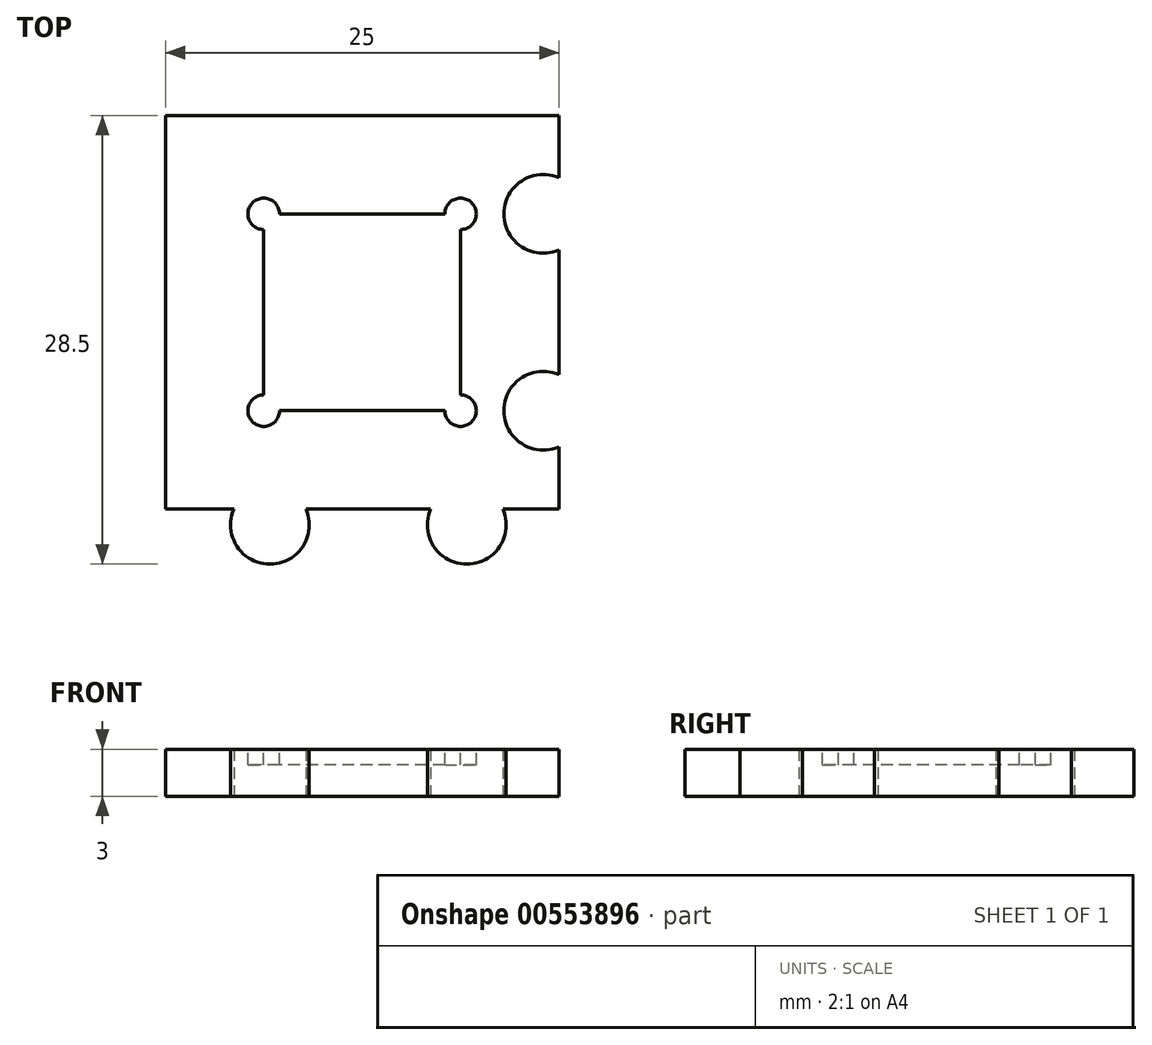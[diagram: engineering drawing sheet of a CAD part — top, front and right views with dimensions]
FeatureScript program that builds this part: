
annotation { "Feature Type Name" : "Feature", "Feature Type Description" : "" }
export const myFeature = defineFeature(function(context is Context, id is Id, definition is map)
    precondition{}
    {
        {
            var Q0;
            Q0=qCreatedBy(makeId("Top.planeOp"),FACE);
            var sketch = newSketch(context, id + "F0", { "sketchPlane" : qUnion([Q0])});
            skLineSegment(sketch, "E0.bottom", {"start": v(12.5, 12.5) * mm, "end": v(-12.5, 12.5) * mm});
            skLineSegment(sketch, "E0.top", {"start": v(12.5, -12.5) * mm, "end": v(-12.5, -12.5) * mm});
            skLineSegment(sketch, "E0.left", {"start": v(12.5, 12.5) * mm, "end": v(12.5, -12.5) * mm});
            skLineSegment(sketch, "E0.right", {"start": v(-12.5, 12.5) * mm, "end": v(-12.5, -12.5) * mm});
            skPoint(sketch, "E0.middle", {"position": v(0, 0) * mm});
            skCircle(sketch, "E1", {"center": v(-5.86, -13.5) * mm, "radius": 2.5 * mm});
            skCircle(sketch, "E2.1.0.0", {"center": v(6.64, -13.5) * mm, "radius": 2.5 * mm});
            skLineSegment(sketch, "E2.direction1", {"start": v(-5.86, -13.5) * mm, "end": v(6.64, -13.5) * mm, "construction": true});
            skSolve(sketch);
        }
        {
            var Q0;
            Q0=qSketchRegion(id+"F0",true);
            extrude(context, id + "F1", {"entities" : qUnion([Q0]), "depth" : 3 * mm, "offsetDistance" : 25 * mm});
        }
        {
            var Q0;
            Q0=makeQuery(id+"F1.opExtrude","CAP_FACE",FACE,{"disambiguationData":[OSD([sQuery(id+"F0.wireOp",EDGE,"E0.bottom"),sQuery(id+"F0.wireOp",EDGE,"E0.top"),sQuery(id+"F0.wireOp",EDGE,"E0.left"),sQuery(id+"F0.wireOp",EDGE,"E0.right")])],"isStart":false});
            var sketch = newSketch(context, id + "F2", { "sketchPlane" : qUnion([Q0])});
            skLineSegment(sketch, "E3.bottom", {"start": v(6.25, 6.25) * mm, "end": v(-6.25, 6.25) * mm});
            skLineSegment(sketch, "E3.top", {"start": v(6.25, -6.25) * mm, "end": v(-6.25, -6.25) * mm});
            skLineSegment(sketch, "E3.left", {"start": v(6.25, 6.25) * mm, "end": v(6.25, -6.25) * mm});
            skLineSegment(sketch, "E3.right", {"start": v(-6.25, 6.25) * mm, "end": v(-6.25, -6.25) * mm});
            skPoint(sketch, "E3.middle", {"position": v(0, 0) * mm});
            skCircle(sketch, "E4", {"center": v(-6.25, 6.25) * mm, "radius": 1 * mm});
            skCircle(sketch, "E5.0.1.0", {"center": v(-6.25, -6.25) * mm, "radius": 1 * mm});
            skCircle(sketch, "E5.1.0.0", {"center": v(6.25, 6.25) * mm, "radius": 1 * mm});
            skCircle(sketch, "E5.1.1.0", {"center": v(6.25, -6.25) * mm, "radius": 1 * mm});
            skLineSegment(sketch, "E5.direction1", {"start": v(-6.25, 6.25) * mm, "end": v(6.25, 6.25) * mm, "construction": true});
            skLineSegment(sketch, "E5.direction2", {"start": v(-6.25, 6.25) * mm, "end": v(-6.25, -6.25) * mm, "construction": true});
            skSolve(sketch);
        }
        {
            var Q0;
            {var subQ5=sQuery(id+"F2.wireOp",EDGE,"E5.1.0.0");var subQ13=sQuery(id+"F2.wireOp",EDGE,"E3.bottom");var subQ14=makeQuery(id+"F2.imprint","INTERSECT",VERTEX,{"derivedFrom":[subQ13,subQ5]});Q0=makeQuery(id+"F2.imprint","IMPRINT",FACE,{"disambiguationData":[TD([[makeQuery(id+"F2.imprint","IMPRINT",EDGE,{"disambiguationData":[TD([[subQ14,-1.0]])],"derivedFrom":subQ13}),1.0]])]});}
            var Q1;
            {var subQ0=sQuery(id+"F2.wireOp",EDGE,"E3.right");var subQ1=sQuery(id+"F2.wireOp",EDGE,"E3.bottom");var subQ2=makeQuery(id+"F2.imprint","INTERSECT",VERTEX,{"derivedFrom":[subQ1,subQ0]});Q1=makeQuery(id+"F2.imprint","IMPRINT",FACE,{"disambiguationData":[TD([[makeQuery(id+"F2.imprint","IMPRINT",EDGE,{"disambiguationData":[TD([[subQ2,1.0]])],"derivedFrom":subQ1}),1.0]])]});}
            var Q2;
            {var subQ0=sQuery(id+"F2.wireOp",EDGE,"E3.right");var subQ1=sQuery(id+"F2.wireOp",EDGE,"E3.bottom");var subQ2=makeQuery(id+"F2.imprint","INTERSECT",VERTEX,{"derivedFrom":[subQ1,subQ0]});Q2=makeQuery(id+"F2.imprint","IMPRINT",FACE,{"disambiguationData":[TD([[makeQuery(id+"F2.imprint","IMPRINT",EDGE,{"disambiguationData":[TD([[subQ2,1.0]])],"derivedFrom":subQ1}),-1.0]])]});}
            var Q3;
            {var subQ0=sQuery(id+"F2.wireOp",EDGE,"E3.left");var subQ1=sQuery(id+"F2.wireOp",EDGE,"E3.bottom");var subQ2=makeQuery(id+"F2.imprint","INTERSECT",VERTEX,{"derivedFrom":[subQ1,subQ0]});Q3=makeQuery(id+"F2.imprint","IMPRINT",FACE,{"disambiguationData":[TD([[makeQuery(id+"F2.imprint","IMPRINT",EDGE,{"disambiguationData":[TD([[subQ2,-1.0]])],"derivedFrom":subQ1}),-1.0]])]});}
            var Q4;
            {var subQ0=sQuery(id+"F2.wireOp",EDGE,"E3.left");var subQ1=sQuery(id+"F2.wireOp",EDGE,"E3.bottom");var subQ2=makeQuery(id+"F2.imprint","INTERSECT",VERTEX,{"derivedFrom":[subQ1,subQ0]});Q4=makeQuery(id+"F2.imprint","IMPRINT",FACE,{"disambiguationData":[TD([[makeQuery(id+"F2.imprint","IMPRINT",EDGE,{"disambiguationData":[TD([[subQ2,-1.0]])],"derivedFrom":subQ1}),1.0]])]});}
            var Q5;
            {var subQ0=sQuery(id+"F2.wireOp",EDGE,"E3.left");var subQ1=sQuery(id+"F2.wireOp",EDGE,"E3.top");var subQ2=makeQuery(id+"F2.imprint","INTERSECT",VERTEX,{"derivedFrom":[subQ1,subQ0]});Q5=makeQuery(id+"F2.imprint","IMPRINT",FACE,{"disambiguationData":[TD([[makeQuery(id+"F2.imprint","IMPRINT",EDGE,{"disambiguationData":[TD([[subQ2,-1.0]])],"derivedFrom":subQ1}),-1.0]])]});}
            var Q6;
            {var subQ0=sQuery(id+"F2.wireOp",EDGE,"E3.left");var subQ1=sQuery(id+"F2.wireOp",EDGE,"E3.top");var subQ2=makeQuery(id+"F2.imprint","INTERSECT",VERTEX,{"derivedFrom":[subQ1,subQ0]});Q6=makeQuery(id+"F2.imprint","IMPRINT",FACE,{"disambiguationData":[TD([[makeQuery(id+"F2.imprint","IMPRINT",EDGE,{"disambiguationData":[TD([[subQ2,-1.0]])],"derivedFrom":subQ1}),1.0]])]});}
            var Q7;
            {var subQ0=sQuery(id+"F2.wireOp",EDGE,"E3.right");var subQ1=sQuery(id+"F2.wireOp",EDGE,"E3.top");var subQ2=makeQuery(id+"F2.imprint","INTERSECT",VERTEX,{"derivedFrom":[subQ1,subQ0]});Q7=makeQuery(id+"F2.imprint","IMPRINT",FACE,{"disambiguationData":[TD([[makeQuery(id+"F2.imprint","IMPRINT",EDGE,{"disambiguationData":[TD([[subQ2,1.0]])],"derivedFrom":subQ1}),-1.0]])]});}
            var Q8;
            {var subQ0=sQuery(id+"F2.wireOp",EDGE,"E3.right");var subQ1=sQuery(id+"F2.wireOp",EDGE,"E3.top");var subQ2=makeQuery(id+"F2.imprint","INTERSECT",VERTEX,{"derivedFrom":[subQ1,subQ0]});Q8=makeQuery(id+"F2.imprint","IMPRINT",FACE,{"disambiguationData":[TD([[makeQuery(id+"F2.imprint","IMPRINT",EDGE,{"disambiguationData":[TD([[subQ2,1.0]])],"derivedFrom":subQ1}),1.0]])]});}
            extrude(context, id + "F3", {"entities" : qUnion([Q0, Q1, Q2, Q3, Q4, Q5, Q6, Q7, Q8]), "operationType" : NewBodyOperationType.REMOVE, "oppositeDirection" : true, "depth" : 1 * mm, "offsetDistance" : 25 * mm});
        }
        {
            var Q0;
            Q0=qCreatedBy(makeId("Top.planeOp"),FACE);
            var sketch = newSketch(context, id + "F4", { "sketchPlane" : qUnion([Q0])});
            skCircle(sketch, "E6", {"center": v(11.5, -6.25) * mm, "radius": 2.5 * mm});
            skCircle(sketch, "E7.0.1.0", {"center": v(11.5, 6.25) * mm, "radius": 2.5 * mm});
            skLineSegment(sketch, "E7.direction1", {"start": v(11.5, -6.25) * mm, "end": v(38.5, -6.25) * mm, "construction": true});
            skLineSegment(sketch, "E7.direction2", {"start": v(11.5, -6.25) * mm, "end": v(11.5, 6.25) * mm, "construction": true});
            skSolve(sketch);
        }
        {
            var Q0;
            Q0=makeQuery(id+"F4.imprint","IMPRINT",FACE,{"disambiguationData":[TD([[makeQuery(id+"F4.imprint","IMPRINT",EDGE,{"derivedFrom":sQuery(id+"F4.wireOp",EDGE,"E7.0.1.0")}),1.0]])]});
            var Q1;
            Q1=makeQuery(id+"F4.imprint","IMPRINT",FACE,{"disambiguationData":[TD([[makeQuery(id+"F4.imprint","IMPRINT",EDGE,{"derivedFrom":sQuery(id+"F4.wireOp",EDGE,"E6")}),1.0]])]});
            extrude(context, id + "F5", {"entities" : qUnion([Q0, Q1]), "operationType" : NewBodyOperationType.REMOVE, "oppositeDirection" : true, "depth" : 3 * mm, "offsetDistance" : 25 * mm});
        }
        {
            var Q0;
            Q0=makeQuery(id+"F4.imprint","IMPRINT",FACE,{"disambiguationData":[TD([[makeQuery(id+"F4.imprint","IMPRINT",EDGE,{"derivedFrom":sQuery(id+"F4.wireOp",EDGE,"E7.0.1.0")}),1.0]])]});
            var Q1;
            Q1=makeQuery(id+"F4.imprint","IMPRINT",FACE,{"disambiguationData":[TD([[makeQuery(id+"F4.imprint","IMPRINT",EDGE,{"derivedFrom":sQuery(id+"F4.wireOp",EDGE,"E6")}),1.0]])]});
            extrude(context, id + "F6", {"entities" : qUnion([Q0, Q1]), "depth" : 3 * mm, "offsetDistance" : 25 * mm});
        }
        {
            var Q0;
            Q0=makeQuery(id+"F6.opExtrude","SWEPT_BODY",BODY,{"disambiguationData":[OSD([sQuery(id+"F4.wireOp",EDGE,"E6")])]});
            var Q1;
            Q1=makeQuery(id+"F6.opExtrude","SWEPT_BODY",BODY,{"disambiguationData":[OSD([sQuery(id+"F4.wireOp",EDGE,"E7.0.1.0")])]});
            var Q2;
            Q2=makeQuery(id+"F1.opExtrude","SWEPT_BODY",BODY,{"disambiguationData":[OSD([sQuery(id+"F0.wireOp",EDGE,"E0.bottom"),sQuery(id+"F0.wireOp",EDGE,"E0.top"),sQuery(id+"F0.wireOp",EDGE,"E0.left"),sQuery(id+"F0.wireOp",EDGE,"E0.right"),sQuery(id+"F0.wireOp",EDGE,"E1"),sQuery(id+"F0.wireOp",EDGE,"E2.1.0.0")])]});
            booleanBodies(context, id + "F7", {"operationType" : BooleanOperationType.SUBTRACTION, "tools" : qUnion([Q0, Q1]), "targets" : qUnion([Q2])});
        }
    });
